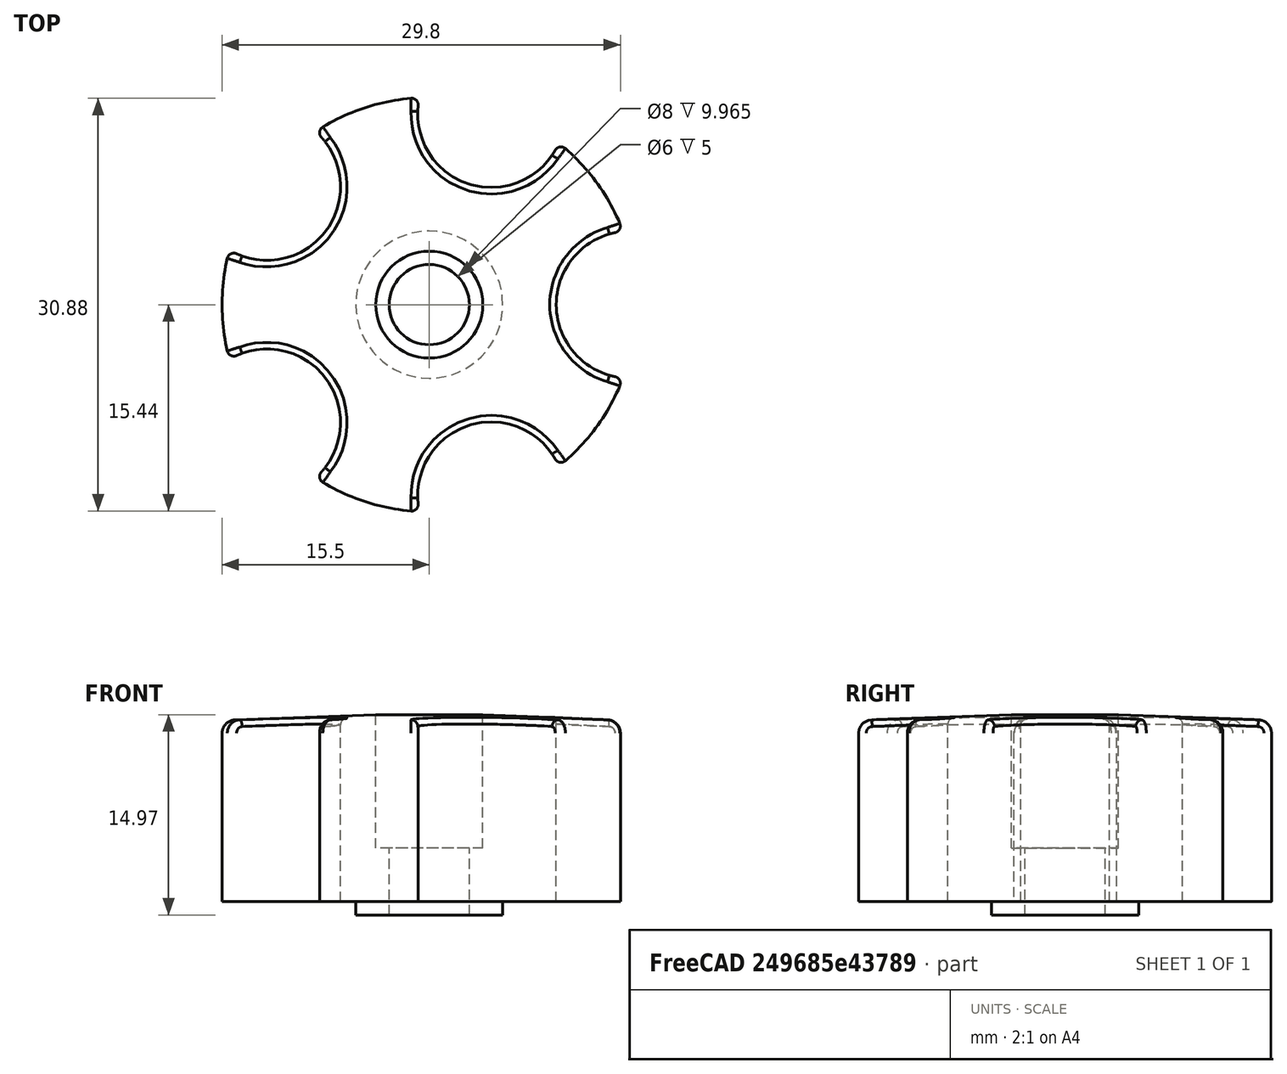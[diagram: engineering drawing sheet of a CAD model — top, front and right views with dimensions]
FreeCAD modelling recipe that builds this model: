
FCSTD DOCUMENT  (FreeCAD 0.19R24276 (Git))
Label: tuerca apriete manual
License: All rights reserved
LicenseURL: http://en.wikipedia.org/wiki/All_rights_reserved
objects: TechDraw::DrawViewDimension×12, Part::Fillet×10, Part::Cylinder×4, Part::Cut×3, TechDraw::DrawSVGTemplate×2, TechDraw::DrawViewPart×2, TechDraw::DrawProjGroupItem×2, TechDraw::DrawPage×2, Sketcher::SketchObject×1, PartDesign::Revolution×1, Part::FeaturePython×1, Part::MultiFuse×1, TechDraw::DrawProjGroup×1, TechDraw::DrawViewAnnotation×1
note: 22 computed .brp shape members not serialized (recipe doc carries the construction recipe); baked Part::Feature solids carry a one-line shape summary decoded from their .brp

FEATURE [Sketcher::SketchObject] Sketch
  FullyConstrained = false
  MapMode = 5
  Placement = pos=(0,0,0) rot=(1,0,0;1.5708rad)
  sketch-geometry (5):
    g0: LineSegment StartX=3 StartY=0 StartZ=0 EndX=3 EndY=14 EndZ=0
    g1: LineSegment StartX=3 StartY=14 StartZ=0 EndX=15.5 EndY=13.5635 EndZ=0
    g2: LineSegment StartX=15.5 StartY=13.5635 StartZ=0 EndX=15.5 EndY=0 EndZ=0
    g3: LineSegment StartX=15.5 StartY=0 StartZ=0 EndX=3 EndY=0 EndZ=0
    g4: LineSegment StartX=0 StartY=0 StartZ=0 EndX=3 EndY=0 EndZ=0
  constraints (14):
    c: Coincident(g0,g1)
    c: Coincident(g1,g2)
    c: Coincident(g2,g3)
    c: Horizontal(g3)
    c: Vertical(g0)
    c: Vertical(g2)
    c: Coincident(g3,g0)
    c: DistanceX(g3,g3) = 12.5
    c: DistanceY(g0,g0) = 14
    c: Angle(g1,g2) = 1.6057
    c: Horizontal(g4)
    c: Coincident(g4,g0)
    c: Coincident(g4,g-1)
    c: DistanceX(g4,g4) = 3
FEATURE [PartDesign::Revolution] Revolution
  AllowMultiFace = false
  Angle = 360
  Axis = (0,0,1)
  Base = (0,0,0)
  Placement = pos=(0,0,0) rot=(1,0,0;1.5708rad)
  Profile = -> Sketch
  ReferenceAxis = -> Sketch [V_Axis]
  Reversed = true
FEATURE [Part::Cylinder] Cylinder  label="Cilindro"
  Angle = 360
  AttacherType = Attacher::AttachEngine3D
  Height = 1
  Placement = pos=(0,0,-1) rot=(0,0,1;0rad)
  Radius = 5.5
FEATURE [Part::Cylinder] Cylinder001  label="Cilindro001"
  Angle = 360
  AttacherType = Attacher::AttachEngine3D
  Height = 1
  Placement = pos=(0,0,-1) rot=(0,0,1;0rad)
  Radius = 3
FEATURE [Part::Cut] Cut
  Base = -> Cylinder
  Tool = -> Cylinder001
FEATURE [Part::Cylinder] Cylinder002  label="Cilindro002"
  Angle = 360
  AttacherType = Attacher::AttachEngine3D
  Height = 10
  Placement = pos=(0,0,4) rot=(0,0,1;0rad)
  Radius = 4
FEATURE [Part::Cut] Cut001
  Base = -> Revolution
  Tool = -> Cylinder002
FEATURE [Part::Cylinder] Cylinder003  label="Cilindro003"
  Angle = 360
  AttacherType = Attacher::AttachEngine3D
  Height = 15
  Placement = pos=(15,0,0) rot=(0,0,1;0rad)
  Radius = 5.5
FEATURE [Part::FeaturePython] Array  # Draft array (typed FeaturePython)
  Angle = 360
  ArrayType = 1
  Axis = (0,0,1)
  Base = -> Cylinder003
  Center = (0,0,0)
  Fuse = false
  IntervalAxis = (0,0,0)
  IntervalX = (1,0,0)
  IntervalY = (0,1,0)
  IntervalZ = (0,0,0)
  NumberPolar = 5
  NumberX = 0
  NumberY = 2
  NumberZ = 1
FEATURE [Part::Cut] Cut002
  Base = -> Cut001
  Tool = -> Array
FEATURE [Part::Fillet] Fillet
  Base = -> Cut002
  Edges = 1 edges r=1: [Edge21]
FEATURE [Part::Fillet] Fillet001
  Base = -> Fillet
  Edges = 1 edges r=1: [Edge30]
FEATURE [Part::Fillet] Fillet002
  Base = -> Fillet001
  Edges = 1 edges r=1: [Edge25]
FEATURE [Part::Fillet] Fillet003
  Base = -> Fillet002
  Edges = 1 edges r=1: [Edge6]
FEATURE [Part::Fillet] Fillet004
  Base = -> Fillet003
  Edges = 1 edges r=1: [Edge6]
FEATURE [Part::Fillet] Fillet005
  Base = -> Fillet004
  Edges = 1 edges r=0.5: [Edge35]
FEATURE [Part::Fillet] Fillet006
  Base = -> Fillet005
  Edges = 1 edges r=0.5: [Edge45]
FEATURE [Part::Fillet] Fillet007
  Base = -> Fillet006
  Edges = 1 edges r=0.5: [Edge27]
FEATURE [Part::Fillet] Fillet008
  Base = -> Fillet007
  Edges = 1 edges r=0.5: [Edge30]
FEATURE [Part::Fillet] Fillet009
  Base = -> Fillet008
  Edges = 1 edges r=0.5: [Edge31]
FEATURE [Part::MultiFuse] Fusion
  Shapes = -> [Fillet009,Cut]
FEATURE [TechDraw::DrawSVGTemplate] Template
  EditableTexts = Designed_by_Name=<owner>; Drawing_number=001; FC-Date=-; FC-SC=2:1; FC-SH=7/10; FC-Title=KnobNut; Subtitle=Tuerca Apriete; Weight=<100gr
  Height = 210
  Orientation = 1
  Width = 297
FEATURE [TechDraw::DrawSVGTemplate] Template001
  EditableTexts = Designed_by_Name=Imepul; Drawing_number=001; FC-Date=-; FC-SC=3:1; FC-SH=8/10; FC-Title=KnobNut; Subtitle=Tuerca Apriete; Weight=<100gr
  Height = 210
  Orientation = 1
  Width = 297
FEATURE [TechDraw::DrawViewPart] View
  CoarseView = false
  Direction = (0.577,-0.577,0.577)
  Focus = 100
  HardHidden = false
  IsoCount = 0
  IsoHidden = false
  IsoVisible = false
  LockPosition = false
  Perspective = false
  Rotation = 0
  Scale = 3
  ScaleType = 0
  SeamHidden = false
  SeamVisible = true
  SmoothHidden = false
  SmoothVisible = true
  Source = -> [Fusion]
  X = 214.5
  XDirection = (0.707,0.707,0)
  Y = 128.6
FEATURE [TechDraw::DrawViewPart] View001
  CoarseView = false
  Direction = (0.577,-0.577,0.577)
  Focus = 100
  HardHidden = false
  IsoCount = 0
  IsoHidden = false
  IsoVisible = false
  LockPosition = false
  Perspective = false
  Rotation = 0
  Scale = 3
  ScaleType = 0
  SeamHidden = false
  SeamVisible = true
  SmoothHidden = false
  SmoothVisible = true
  Source = -> [Fusion]
  X = 147.828
  XDirection = (0.707,0.707,0)
  Y = 131.118
FEATURE [TechDraw::DrawProjGroupItem] ProjItem  label="Front"
  CoarseView = false
  Direction = (0,-1,0)
  Focus = 100
  HardHidden = false
  IsoCount = 0
  IsoHidden = false
  IsoVisible = false
  LockPosition = true
  Perspective = false
  Rotation = 0
  RotationVector = (1,0,0)
  Scale = 2
  ScaleType = 2
  SeamHidden = false
  SeamVisible = true
  SmoothHidden = false
  SmoothVisible = true
  Source = -> [Fusion]
  Type = 0
  X = 0
  XDirection = (1,0,0)
  Y = 0
FEATURE [TechDraw::DrawProjGroupItem] ProjItem002  label="Top"
  CoarseView = false
  Direction = (0,0,1)
  Focus = 100
  HardHidden = false
  IsoCount = 0
  IsoHidden = false
  IsoVisible = false
  LockPosition = false
  Perspective = false
  Rotation = 0
  RotationVector = (1,0,0)
  Scale = 2
  ScaleType = 2
  SeamHidden = false
  SeamVisible = true
  SmoothHidden = false
  SmoothVisible = true
  Source = -> [Fusion]
  Type = 4
  X = 0
  XDirection = (1,0,0)
  Y = -75.408
FEATURE [TechDraw::DrawProjGroup] ProjGroup
  Anchor = -> ProjItem
  AutoDistribute = true
  LockPosition = false
  ProjectionType = 0
  Rotation = 0
  Scale = 2
  ScaleType = 2
  Source = -> [Fusion]
  Views = -> [ProjItem,ProjItem002]
  X = 97.7
  Y = 162.2
  spacingX = 15
  spacingY = 15
FEATURE [TechDraw::DrawViewDimension] Dimension
  Arbitrary = false
  ArbitraryTolerances = false
  EqualTolerance = true
  FormatSpec = %.2f
  FormatSpecOverTolerance = %+.2f
  FormatSpecUnderTolerance = %+.2f
  Inverted = false
  LockPosition = false
  MeasureType = 1
  OverTolerance = 0
  References2D = -> [ProjItem]
  Rotation = 0
  ScaleType = 0
  TheoreticalExact = false
  Type = 1
  UnderTolerance = 0
  X = -2.53975
  Y = -18.7234
FEATURE [TechDraw::DrawViewDimension] Dimension001
  Arbitrary = false
  ArbitraryTolerances = false
  EqualTolerance = true
  FormatSpec = %.2f
  FormatSpecOverTolerance = %+.2f
  FormatSpecUnderTolerance = %+.2f
  Inverted = false
  LockPosition = false
  MeasureType = 1
  OverTolerance = 0
  References2D = -> [ProjItem]
  Rotation = 0
  ScaleType = 0
  TheoreticalExact = false
  Type = 2
  UnderTolerance = 0
  X = 41.3306
  Y = -24.2049
FEATURE [TechDraw::DrawViewDimension] Dimension002
  Arbitrary = false
  ArbitraryTolerances = false
  EqualTolerance = true
  FormatSpec = %.2f
  FormatSpecOverTolerance = %+.2f
  FormatSpecUnderTolerance = %+.2f
  Inverted = false
  LockPosition = false
  MeasureType = 1
  OverTolerance = 0
  References2D = -> [ProjItem]
  Rotation = 0
  ScaleType = 0
  TheoreticalExact = false
  Type = 1
  UnderTolerance = 0
  X = -50.5073
  Y = 3.37704
FEATURE [TechDraw::DrawViewDimension] Dimension003
  Arbitrary = false
  ArbitraryTolerances = false
  EqualTolerance = true
  FormatSpec = %.2f
  FormatSpecOverTolerance = %+.2f
  FormatSpecUnderTolerance = %+.2f
  Inverted = false
  LockPosition = false
  MeasureType = 1
  OverTolerance = 0
  References2D = -> [ProjItem]
  Rotation = 0
  ScaleType = 0
  TheoreticalExact = false
  Type = 2
  UnderTolerance = 0
  X = -71.3034
  Y = 21.6534
FEATURE [TechDraw::DrawViewDimension] Dimension005
  Arbitrary = false
  ArbitraryTolerances = false
  EqualTolerance = true
  FormatSpec = ⌀%.2f
  FormatSpecOverTolerance = %+.2f
  FormatSpecUnderTolerance = %+.2f
  Inverted = false
  LockPosition = false
  MeasureType = 1
  OverTolerance = 0
  References2D = -> [ProjItem002]
  Rotation = 0
  ScaleType = 0
  TheoreticalExact = false
  Type = 5
  UnderTolerance = 0
  X = -58.3223
  Y = 0.211313
FEATURE [TechDraw::DrawViewDimension] Dimension006
  Arbitrary = false
  ArbitraryTolerances = false
  EqualTolerance = true
  FormatSpec = ⌀%.2f
  FormatSpecOverTolerance = %+.2f
  FormatSpecUnderTolerance = %+.2f
  Inverted = false
  LockPosition = false
  MeasureType = 1
  OverTolerance = 0
  References2D = -> [View001]
  Rotation = 0
  ScaleType = 0
  TheoreticalExact = false
  Type = 5
  UnderTolerance = 0
  X = -3.95577
  Y = 22.5175
FEATURE [TechDraw::DrawViewDimension] Dimension009
  Arbitrary = false
  ArbitraryTolerances = false
  EqualTolerance = true
  FormatSpec = %.2f
  FormatSpecOverTolerance = %+.2f
  FormatSpecUnderTolerance = %+.2f
  Inverted = false
  LockPosition = false
  MeasureType = 1
  OverTolerance = 0
  References2D = -> [View001]
  Rotation = 0
  ScaleType = 0
  TheoreticalExact = false
  Type = 0
  UnderTolerance = 0
  X = 3.28316
  Y = -41.0926
FEATURE [TechDraw::DrawViewDimension] Dimension010
  Arbitrary = false
  ArbitraryTolerances = false
  EqualTolerance = true
  FormatSpec = %.2f
  FormatSpecOverTolerance = %+.2f
  FormatSpecUnderTolerance = %+.2f
  Inverted = false
  LockPosition = false
  MeasureType = 1
  OverTolerance = 0
  References2D = -> [View001]
  Rotation = 0
  ScaleType = 0
  TheoreticalExact = false
  Type = 0
  UnderTolerance = 0
  X = 32.4185
  Y = -8.14291
FEATURE [TechDraw::DrawViewDimension] Dimension011
  Arbitrary = false
  ArbitraryTolerances = false
  EqualTolerance = true
  FormatSpec = %.2f
  FormatSpecOverTolerance = %+.2f
  FormatSpecUnderTolerance = %+.2f
  Inverted = false
  LockPosition = false
  MeasureType = 1
  OverTolerance = 0
  References2D = -> [View001]
  Rotation = 0
  ScaleType = 0
  TheoreticalExact = false
  Type = 0
  UnderTolerance = 0
  X = -33.1484
  Y = -14.4236
FEATURE [TechDraw::DrawViewDimension] Dimension012
  Arbitrary = false
  ArbitraryTolerances = false
  EqualTolerance = true
  FormatSpec = %.2f
  FormatSpecOverTolerance = %+.2f
  FormatSpecUnderTolerance = %+.2f
  Inverted = false
  LockPosition = false
  MeasureType = 1
  OverTolerance = 0
  References2D = -> [View001]
  Rotation = 0
  ScaleType = 0
  TheoreticalExact = false
  Type = 0
  UnderTolerance = 0
  X = 18.2183
  Y = 23.4311
FEATURE [TechDraw::DrawViewDimension] Dimension013
  Arbitrary = false
  ArbitraryTolerances = false
  EqualTolerance = true
  FormatSpec = %.2f
  FormatSpecOverTolerance = %+.2f
  FormatSpecUnderTolerance = %+.2f
  Inverted = false
  LockPosition = false
  MeasureType = 1
  OverTolerance = 0
  References2D = -> [View001]
  Rotation = 0
  ScaleType = 0
  TheoreticalExact = false
  Type = 1
  UnderTolerance = 0
  X = -25.4496
  Y = -33.8791
FEATURE [TechDraw::DrawViewDimension] Dimension014
  Arbitrary = false
  ArbitraryTolerances = false
  EqualTolerance = true
  FormatSpec = ⌀%.2f
  FormatSpecOverTolerance = %+.2f
  FormatSpecUnderTolerance = %+.2f
  Inverted = false
  LockPosition = false
  MeasureType = 1
  OverTolerance = 0
  References2D = -> [ProjItem002]
  Rotation = 0
  ScaleType = 0
  TheoreticalExact = false
  Type = 5
  UnderTolerance = 0
  X = -28.8
  Y = -42.4
FEATURE [TechDraw::DrawPage] Page  label="Vistas"
  KeepUpdated = true
  NextBalloonIndex = 1
  ProjectionType = 0
  Template = -> Template
  Views = -> [View,ProjGroup,Dimension,Dimension001,Dimension002,Dimension003,Dimension005,Dimension014]
FEATURE [TechDraw::DrawViewAnnotation] Annotation
  Font = osifont
  LineSpace = 80
  LockPosition = false
  MaxWidth = -1
  Rotation = 0
  ScaleType = 0
  Text = Aproximate measurements: | Check with 3D piece
  TextSize = 5
  TextStyle = 0
  X = 64.9
  Y = 80.6
FEATURE [TechDraw::DrawPage] Page001  label="Cotas"
  KeepUpdated = true
  NextBalloonIndex = 1
  ProjectionType = 0
  Template = -> Template001
  Views = -> [View001,Dimension006,Dimension009,Dimension010,Dimension011,Dimension012,Dimension013,Annotation]
